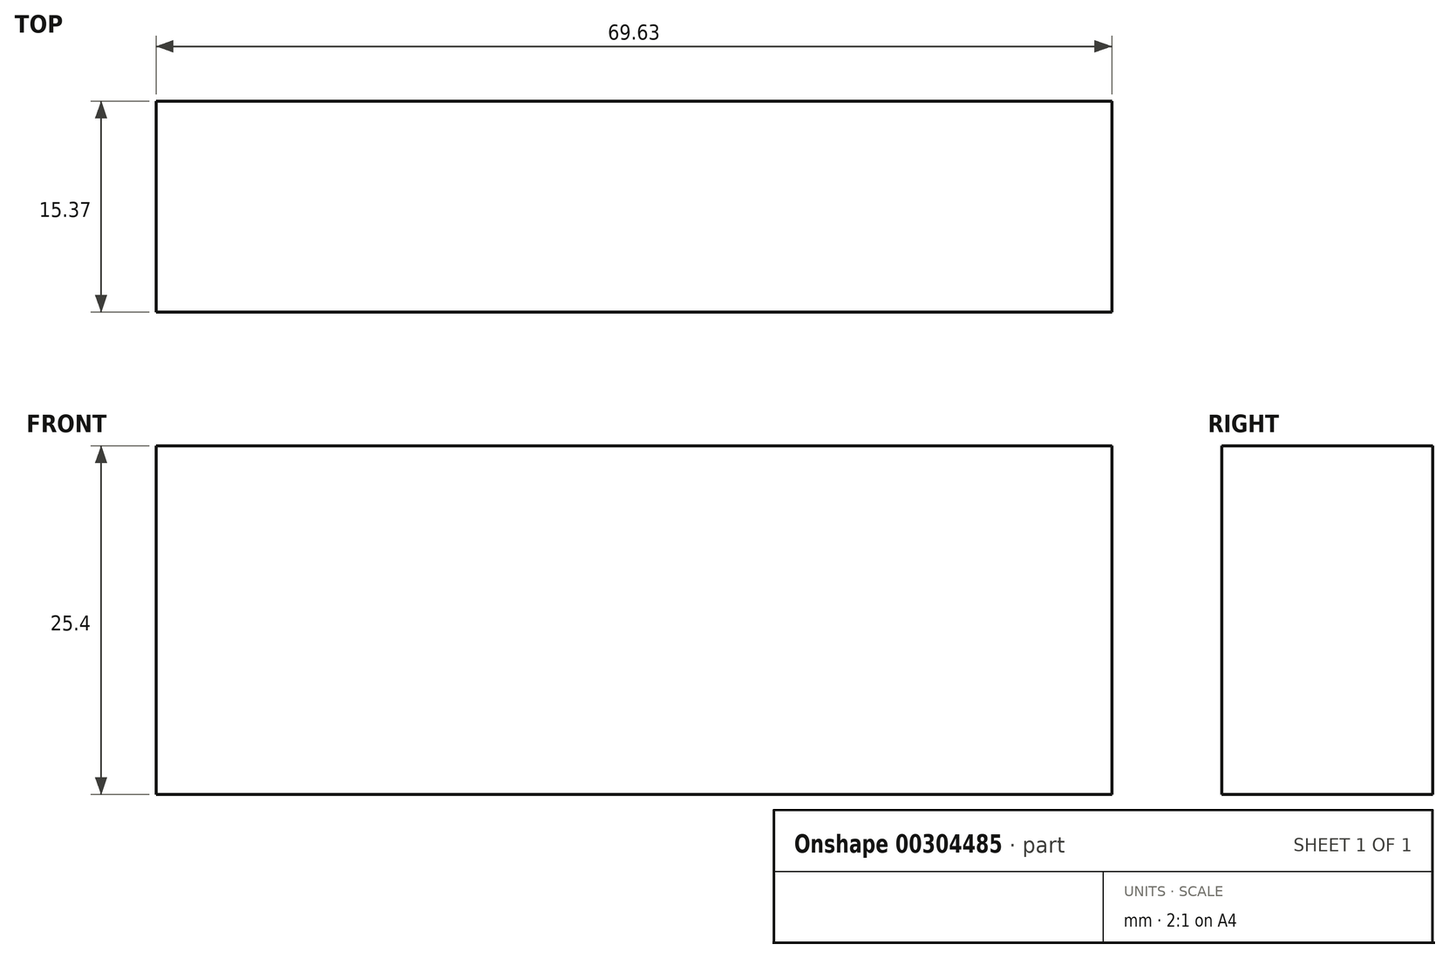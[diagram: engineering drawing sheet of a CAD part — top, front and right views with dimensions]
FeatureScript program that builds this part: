
annotation { "Feature Type Name" : "Feature", "Feature Type Description" : "" }
export const myFeature = defineFeature(function(context is Context, id is Id, definition is map)
    precondition{}
    {
        {
            var Q0;
            Q0=qCreatedBy(makeId("Top.planeOp"),FACE);
            var sketch = newSketch(context, id + "F0", { "sketchPlane" : qUnion([Q0])});
            skLineSegment(sketch, "E0.bottom", {"start": v(-25.24, 15.37) * mm, "end": v(44.4, 15.37) * mm});
            skLineSegment(sketch, "E0.top", {"start": v(-25.24, 0) * mm, "end": v(44.4, 0) * mm});
            skLineSegment(sketch, "E0.left", {"start": v(-25.24, 15.37) * mm, "end": v(-25.24, 0) * mm});
            skLineSegment(sketch, "E0.right", {"start": v(44.4, 15.37) * mm, "end": v(44.4, 0) * mm});
            skSolve(sketch);
        }
        {
            var Q0;
            Q0=makeQuery(id+"F0.imprint","IMPRINT",FACE,{"disambiguationData":[TD([[makeQuery(id+"F0.imprint","IMPRINT",EDGE,{"derivedFrom":sQuery(id+"F0.wireOp",EDGE,"E0.bottom")}),-1.0]])]});
            extrude(context, id + "F1", {"entities" : qUnion([Q0]), "depth" : 25.4 * mm});
        }
    });
